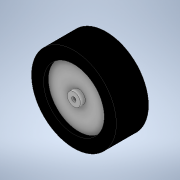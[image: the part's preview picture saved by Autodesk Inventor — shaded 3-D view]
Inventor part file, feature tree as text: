
AUTODESK INVENTOR PART (.ipt)
format: ipt  version: 2020 (Build 240168000, 168)  size: 137,728 bytes
history: native  units: mm
features: extrude x4, sketch x4, other x1, mirror x1
ambient origin geometry x8: Origin, YZ Plane, XZ Plane, XY Plane, X Axis, Y Axis, Z Axis, Center Point
bodies: Body1 (feature_tree)
feature tree (10):
  extrude  "Extrusão2"  Depth=26.6mm TaperAngle=0.0deg
  extrude  "Extrusão5"  Depth=4.0mm TaperAngle=0.0deg
  extrude  "Extrusão7"  Depth=4.0mm TaperAngle=0.0deg
  extrude  "Extrusão8"  TaperAngle=0.0deg  [1 undecoded]
  other  "Plano de trabalho1"
  mirror  "Espelhamento2"
  sketch  "Esboço2"  dims[d5=70.0mm d6=26.6mm d7=0.0mm]
  sketch  "Esboço9"  dims[d18=50.0mm d19=4.0mm d20=0.0mm]
  sketch  "Esboço12"  dims[d24=10.8mm d25=4.0mm d26=0.0mm]
  sketch  "Esboço13"  dims[d27=3.6mm d28=0.0mm d29=0.0mm d35=-13.3mm]
note: 1 required parameter value undecoded (feature->parameter linkage not recoverable at this tier; creation-order binding heuristic only, values carry confidence <= 0.55)
